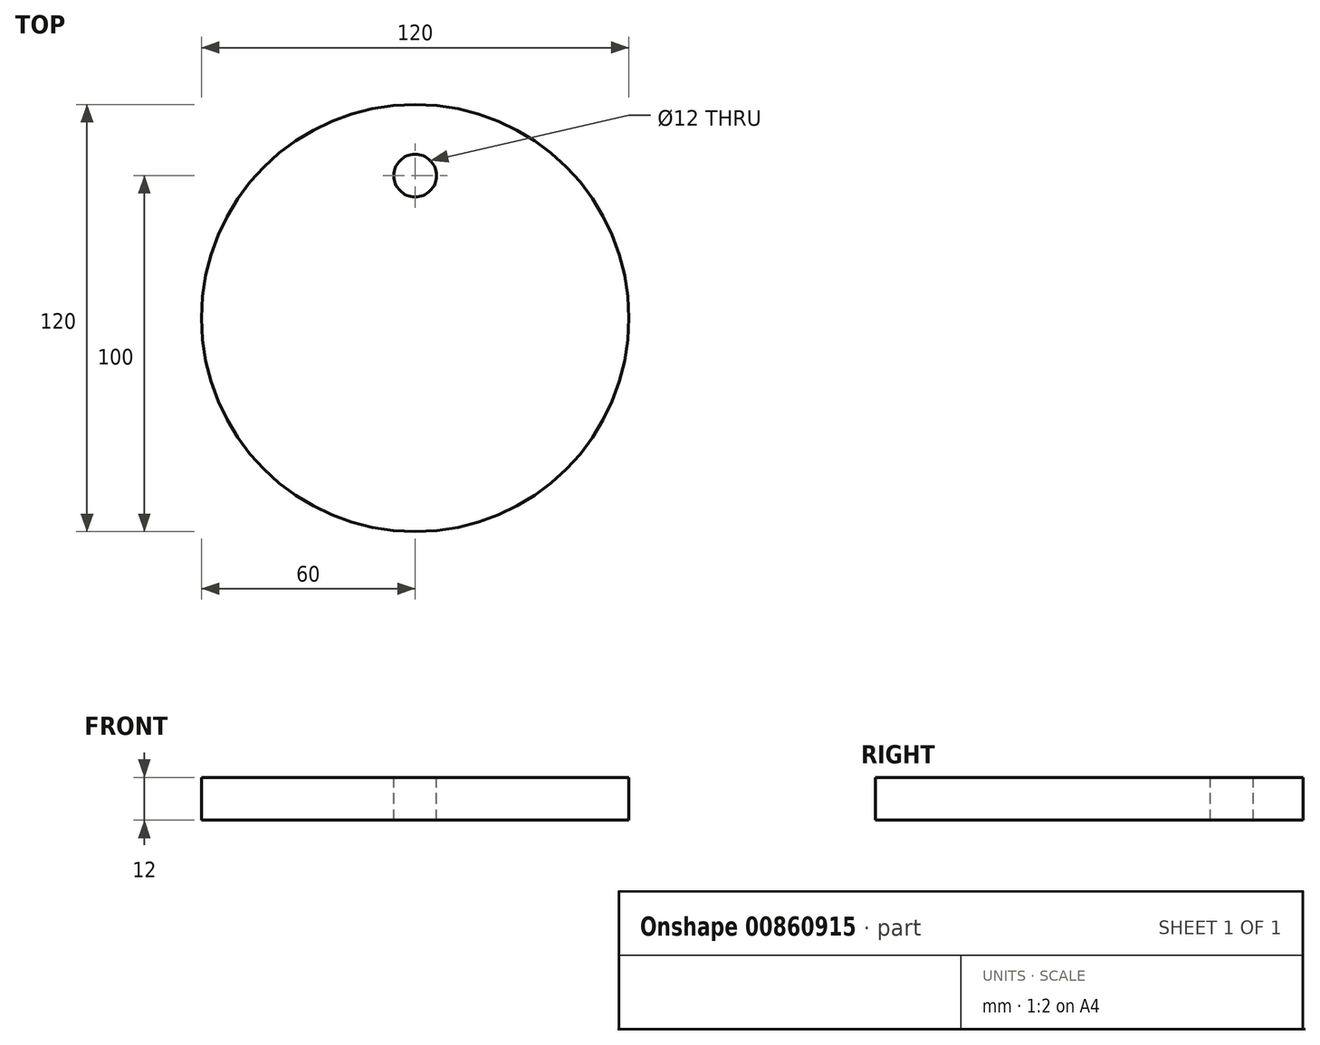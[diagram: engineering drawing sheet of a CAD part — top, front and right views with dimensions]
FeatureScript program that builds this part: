
annotation { "Feature Type Name" : "Feature", "Feature Type Description" : "" }
export const myFeature = defineFeature(function(context is Context, id is Id, definition is map)
    precondition{}
    {
        {
            assignVariable(context, id + "F0", {"name" : "BigCircle", "anyValue" : 120});
        }
        {
            assignVariable(context, id + "F1", {"name" : "Thickness", "anyValue" : getVariable(context, 'BigCircle') / 10});
        }
        {
            var Q0;
            Q0=qCreatedBy(makeId("Top.planeOp"),FACE);
            var sketch = newSketch(context, id + "F2", { "sketchPlane" : qUnion([Q0])});
            skCircle(sketch, "E0", {"center": v(0, 0) * mm, "radius": 60 * mm});
            skSolve(sketch);
        }
        {
            var Q0;
            Q0=makeQuery(id+"F2.imprint","IMPRINT",FACE,{"disambiguationData":[TD([[makeQuery(id+"F2.imprint","IMPRINT",EDGE,{"derivedFrom":sQuery(id+"F2.wireOp",EDGE,"E0")}),1.0]])]});
            extrude(context, id + "F3", {"entities" : qUnion([Q0]), "depth" : (getVariable(context, 'Thickness')) * mm, "offsetDistance" : 25 * mm});
        }
        {
            var Q0;
            Q0=makeQuery(id+"F3.opExtrude","CAP_FACE",FACE,{"disambiguationData":[OSD([sQuery(id+"F2.wireOp",EDGE,"E0")])],"isStart":false});
            var sketch = newSketch(context, id + "F4", { "sketchPlane" : qUnion([Q0])});
            skCircle(sketch, "E1", {"center": v(0, 0) * mm, "radius": 40 * mm, "construction": true});
            skCircle(sketch, "E2", {"center": v(0, 40) * mm, "radius": 6 * mm});
            skSolve(sketch);
        }
        {
            var Q0;
            Q0=makeQuery(id+"F4.imprint","IMPRINT",FACE,{"disambiguationData":[TD([[makeQuery(id+"F4.imprint","IMPRINT",EDGE,{"derivedFrom":sQuery(id+"F4.wireOp",EDGE,"E2")}),1.0]])]});
            extrude(context, id + "F5", {"entities" : qUnion([Q0]), "operationType" : NewBodyOperationType.REMOVE, "endBound" : BoundingType.THROUGH_ALL, "oppositeDirection" : true, "depth" : 25 * mm, "offsetDistance" : 25 * mm});
        }
    });
